# Revit family: MAGIC 1.8 LED LINEAR LIGHT
name_source: partatom
category: Lighting Fixtures
units: mm (PartAtom-declared; Revit-internal decimal feet)

## family parameters
Cut with Voids When Loaded = No
Host = Face
Light Source = Yes
Part Type = Normal
Room Calculation Point = No
Round Connector Dimension = Use Diameter
Shared = No

## types (6) — shared parameters
Average life based on L70(HRS) = 100000
CRI = 80
Color Filter = 16777215
Default Elevation = 4' - 0"
Description = This MAGIC led linear fixture is a 1.8 wide, linear architectural luminaire with a slim and a discrete profile.
Dimming Lamp Color Temperature Shift = <None>
Fixture Height = 0' - 3"
Load Classification = Lighting
Manufacturer = Above All Lighting
Power Factor = 1
Type Comments = MAGIC 1.8 LED LINEAR LIGHT
URL = https://www.abovealllighting.com
Voltage = 277 V

## per-type parameters (varying)
| type | Dimming / Control | Finish/Color | Inside Element | LIGHT LENGTH | Model | Photometric Web File | Tilt Angle | WATTS | Wattage Comments |
| MAG0618-SW1-PSM-SD-FDL | 0 V | <By Category> | <By Category> | 2' - 0" |  | MAG0618-SW1(4000K).IES | -90.00° | 20 W | 20W/15W/10W |
| MAG1218-SW1-PSM-SD-FDL | 10 V | White Aluminum | white inside | 4' - 0" |  | MAG1218-SW1(4000K).IES | -90.00° | 40 W | 40W/30W/20W |
| MAG0618-SW1-WM-SD-FDL | 0 V | <By Category> | <By Category> | 2' - 0" |  | MAG0618-SW1(4000K).IES | 180.00° | 20 W | 20W/15W/10W |
| MAG1218-SW1-WM-SD-FDL | 0 V | <By Category> | <By Category> | 4' - 0" | MAG1218-SW1(4000K)-WM-SD-FDL | MAG1218-SW1(4000K).IES | 180.00° | 40 W | 40W/30W/20W |
| MAG2418-SW1-PSM-SD-FDL | 0 V | <By Category> | <By Category> | 8' - 0" |  | generic.ies | -90.00° | 80 W | 80W/60W/40W |
| MAG2418-SW1-WM-SD-FDL | 0 V | <By Category> | <By Category> | 8' - 0" | MAG1218-SW1(4000K)-WM-SD-FDL | generic.ies | 180.00° | 80 W | 80W/60W/40W |

## geometry (parser evidence)
native form markers: Sweep x8
no freeform markers — native parametric forms only
